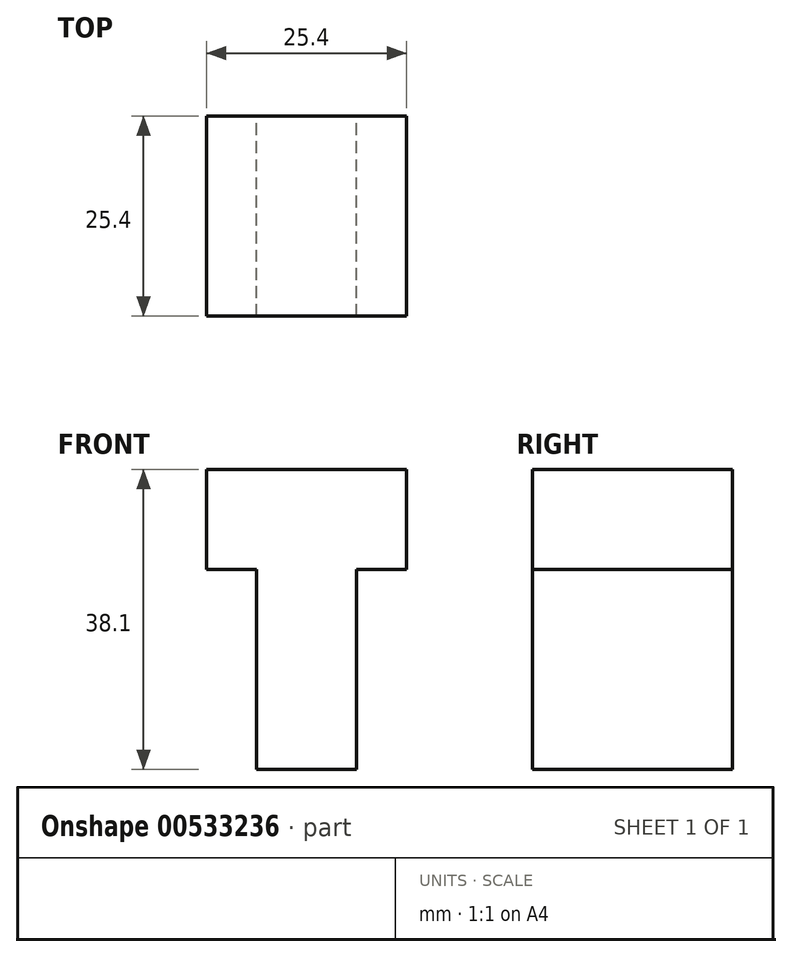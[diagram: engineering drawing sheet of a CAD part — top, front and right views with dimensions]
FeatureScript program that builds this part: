
annotation { "Feature Type Name" : "Feature", "Feature Type Description" : "" }
export const myFeature = defineFeature(function(context is Context, id is Id, definition is map)
    precondition{}
    {
        {
            var Q0;
            Q0=qCreatedBy(makeId("Front.planeOp"),FACE);
            var sketch = newSketch(context, id + "F0", { "sketchPlane" : qUnion([Q0])});
            skLineSegment(sketch, "E0", {"start": v(-56.2, 30.94) * mm, "end": v(-56.2, 5.54) * mm});
            skLineSegment(sketch, "E1", {"start": v(-56.2, 5.54) * mm, "end": v(-43.5, 5.54) * mm});
            skLineSegment(sketch, "E2", {"start": v(-43.5, 5.54) * mm, "end": v(-43.5, 30.94) * mm});
            skLineSegment(sketch, "E3", {"start": v(-43.5, 30.94) * mm, "end": v(-37.15, 30.94) * mm});
            skLineSegment(sketch, "E4", {"start": v(-37.15, 30.94) * mm, "end": v(-37.15, 43.64) * mm});
            skLineSegment(sketch, "E5", {"start": v(-37.15, 43.64) * mm, "end": v(-62.55, 43.64) * mm});
            skLineSegment(sketch, "E6", {"start": v(-62.55, 43.64) * mm, "end": v(-62.55, 30.94) * mm});
            skLineSegment(sketch, "E7", {"start": v(-62.55, 30.94) * mm, "end": v(-56.2, 30.94) * mm});
            skSolve(sketch);
        }
        {
            var Q0;
            Q0=makeQuery(id+"F0.imprint","IMPRINT",FACE,{"disambiguationData":[TD([[makeQuery(id+"F0.imprint","IMPRINT",EDGE,{"derivedFrom":sQuery(id+"F0.wireOp",EDGE,"E0")}),1.0]])]});
            extrude(context, id + "F1", {"entities" : qUnion([Q0]), "depth" : 25.4 * mm, "offsetDistance" : 25.4 * mm});
        }
    });
